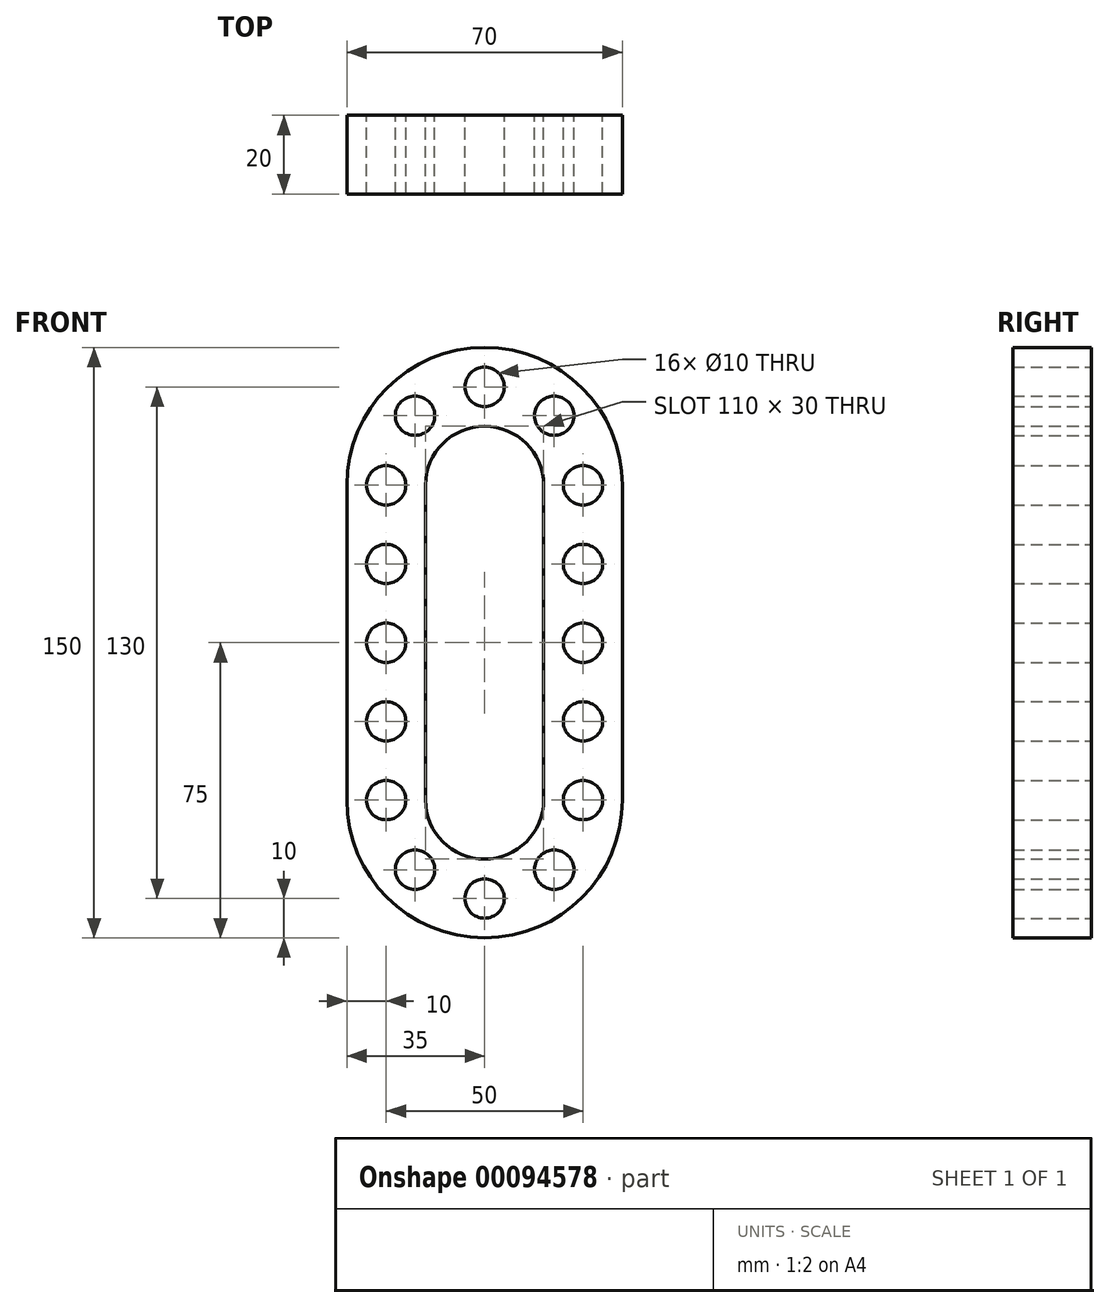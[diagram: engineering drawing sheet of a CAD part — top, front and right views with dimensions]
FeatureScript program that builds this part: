
annotation { "Feature Type Name" : "Feature", "Feature Type Description" : "" }
export const myFeature = defineFeature(function(context is Context, id is Id, definition is map)
    precondition{}
    {
        {
            var Q0;
            Q0=qCreatedBy(makeId("Front.planeOp"),FACE);
            var sketch = newSketch(context, id + "F0", { "sketchPlane" : qUnion([Q0])});
            skPoint(sketch, "E0", {"position": v(-25, 40) * mm});
            skLineSegment(sketch, "E1", {"start": v(-25, 40) * mm, "end": v(-25, 0) * mm, "construction": true});
            skArc(sketch, "E2", {"start": v(0, 65) * mm, "mid": v(-17.68, 57.68) * mm, "end": v(-25, 40) * mm, "construction": true});
            skArc(sketch, "E3.0.startCap", {"start": v(0, 75) * mm, "mid": v(10, 65) * mm, "end": v(0, 55) * mm, "construction": true});
            skArc(sketch, "E3.0.endCap", {"start": v(-15, 40) * mm, "mid": v(-25, 30) * mm, "end": v(-35, 40) * mm, "construction": true});
            skArc(sketch, "E3.0.left", {"start": v(0, 55) * mm, "mid": v(-10.6, 50.6) * mm, "end": v(-15, 40) * mm});
            skArc(sketch, "E3.0.right", {"start": v(0, 75) * mm, "mid": v(-24.75, 64.75) * mm, "end": v(-35, 40) * mm});
            skArc(sketch, "E3.1.startCap", {"start": v(-35, 40) * mm, "mid": v(-25, 50) * mm, "end": v(-15, 40) * mm, "construction": true});
            skArc(sketch, "E3.1.endCap", {"start": v(-15, 0) * mm, "mid": v(-25, -10) * mm, "end": v(-35, 0) * mm, "construction": true});
            skLineSegment(sketch, "E3.1.left", {"start": v(-15, 40) * mm, "end": v(-15, 0) * mm});
            skLineSegment(sketch, "E3.1.right", {"start": v(-35, 40) * mm, "end": v(-35, 0) * mm});
            skCircle(sketch, "E4", {"center": v(-25, 40) * mm, "radius": 5 * mm});
            skCircle(sketch, "E5.0.1.0", {"center": v(-25, 20) * mm, "radius": 5 * mm});
            skArc(sketch, "E5.0.2.0", {"start": v(-20, 0) * mm, "mid": v(-25, 5) * mm, "end": v(-30, 0) * mm});
            skLineSegment(sketch, "E5.direction1", {"start": v(-25, 40) * mm, "end": v(0, 40) * mm, "construction": true});
            skLineSegment(sketch, "E5.direction2", {"start": v(-25, 40) * mm, "end": v(-25, 20) * mm, "construction": true});
            skCircle(sketch, "E6.1.0", {"center": v(-17.68, 57.68) * mm, "radius": 5 * mm});
            skArc(sketch, "E6.2.0", {"start": v(0, 70) * mm, "mid": v(-5, 65) * mm, "end": v(0, 60) * mm});
            skLineSegment(sketch, "E6.anchor1", {"start": v(0, 40) * mm, "end": v(-25, 40) * mm, "construction": true});
            skLineSegment(sketch, "E6.anchor2", {"start": v(0, 40) * mm, "end": v(0, 65) * mm, "construction": true});
            skLineSegment(sketch, "E7", {"start": v(-35, 0) * mm, "end": v(-30, 0) * mm});
            skLineSegment(sketch, "E8", {"start": v(-15, 0) * mm, "end": v(-20, 0) * mm});
            skLineSegment(sketch, "E9", {"start": v(0, 75) * mm, "end": v(0, 70) * mm});
            skLineSegment(sketch, "E10", {"start": v(0, 55) * mm, "end": v(0, 60) * mm});
            skSolve(sketch);
        }
        {
            var Q0;
            Q0 = qSketchRegion(id + "F0", true);
            extrude(context, id + "F1", {"entities" : qUnion([Q0]), "depth" : 20 * mm});
        }
        {
            var Q0;
            Q0=makeQuery(id+"F1.opExtrude","SWEPT_BODY",BODY,{"disambiguationData":[OSD([sQuery(id+"F0.wireOp",EDGE,"E3.0.left"),sQuery(id+"F0.wireOp",EDGE,"E3.0.right"),sQuery(id+"F0.wireOp",EDGE,"E3.1.left"),sQuery(id+"F0.wireOp",EDGE,"E3.1.right"),sQuery(id+"F0.wireOp",EDGE,"E4"),sQuery(id+"F0.wireOp",EDGE,"E5.0.1.0"),sQuery(id+"F0.wireOp",EDGE,"E5.0.2.0"),sQuery(id+"F0.wireOp",EDGE,"E6.1.0"),sQuery(id+"F0.wireOp",EDGE,"E6.2.0"),sQuery(id+"F0.wireOp",EDGE,"E7"),sQuery(id+"F0.wireOp",EDGE,"E8"),sQuery(id+"F0.wireOp",EDGE,"E9"),sQuery(id+"F0.wireOp",EDGE,"E10")])]});
            var Q1;
            Q1=qCreatedBy(makeId("Right.planeOp"),FACE);
            mirror(context, id + "F2", {"operationType" : NewBodyOperationType.ADD, "entities" : qUnion([Q0]), "mirrorPlane" : qUnion([Q1])});
        }
        {
            var Q0;
            Q0=makeQuery(id+"F1.opExtrude","SWEPT_BODY",BODY,{"disambiguationData":[OSD([sQuery(id+"F0.wireOp",EDGE,"E3.0.left"),sQuery(id+"F0.wireOp",EDGE,"E3.0.right"),sQuery(id+"F0.wireOp",EDGE,"E3.1.left"),sQuery(id+"F0.wireOp",EDGE,"E3.1.right"),sQuery(id+"F0.wireOp",EDGE,"E4"),sQuery(id+"F0.wireOp",EDGE,"E5.0.1.0"),sQuery(id+"F0.wireOp",EDGE,"E5.0.2.0"),sQuery(id+"F0.wireOp",EDGE,"E6.1.0"),sQuery(id+"F0.wireOp",EDGE,"E6.2.0"),sQuery(id+"F0.wireOp",EDGE,"E7"),sQuery(id+"F0.wireOp",EDGE,"E8"),sQuery(id+"F0.wireOp",EDGE,"E9"),sQuery(id+"F0.wireOp",EDGE,"E10")])]});
            var Q1;
            Q1=qCreatedBy(makeId("Top.planeOp"),FACE);
            mirror(context, id + "F3", {"operationType" : NewBodyOperationType.ADD, "entities" : qUnion([Q0]), "mirrorPlane" : qUnion([Q1])});
        }
    });
